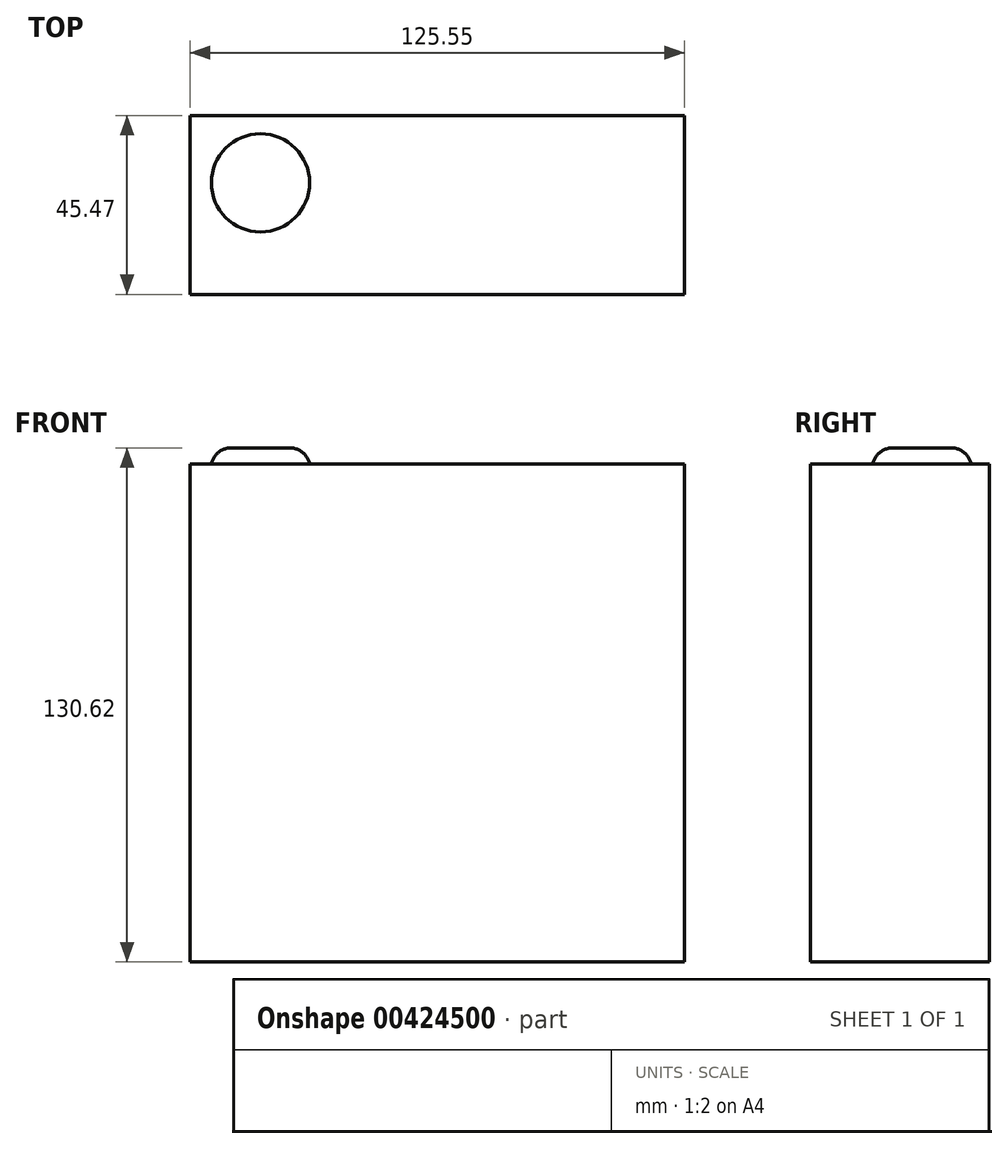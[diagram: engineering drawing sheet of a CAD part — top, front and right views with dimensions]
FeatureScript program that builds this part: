
annotation { "Feature Type Name" : "Feature", "Feature Type Description" : "" }
export const myFeature = defineFeature(function(context is Context, id is Id, definition is map)
    precondition{}
    {
        {
            var Q0;
            Q0=qCreatedBy(makeId("Front.planeOp"),FACE);
            var sketch = newSketch(context, id + "F0", { "sketchPlane" : qUnion([Q0])});
            skLineSegment(sketch, "E0.bottom", {"start": v(-59.76, 61.14) * mm, "end": v(65.8, 61.14) * mm});
            skLineSegment(sketch, "E0.top", {"start": v(-59.76, -65.42) * mm, "end": v(65.8, -65.42) * mm});
            skLineSegment(sketch, "E0.left", {"start": v(-59.76, 61.14) * mm, "end": v(-59.76, -65.42) * mm});
            skLineSegment(sketch, "E0.right", {"start": v(65.8, 61.14) * mm, "end": v(65.8, -65.42) * mm});
            skSolve(sketch);
        }
        {
            var Q0;
            Q0 = qSketchRegion(id + "F0", true);
            extrude(context, id + "F1", {"entities" : qUnion([Q0]), "depth" : 45.47 * mm});
        }
        {
            var Q0;
            Q0=makeQuery(id+"F1.opExtrude","SWEPT_FACE",FACE,{"disambiguationData":[OSD([sQuery(id+"F0.wireOp",EDGE,"E0.bottom")])]});
            var sketch = newSketch(context, id + "F2", { "sketchPlane" : qUnion([Q0])});
            skCircle(sketch, "E1", {"center": v(-41.9, -17.1) * mm, "radius": 12.47 * mm});
            skSolve(sketch);
        }
        {
            var Q0;
            Q0 = qSketchRegion(id + "F2", true);
            extrude(context, id + "F3", {"entities" : qUnion([Q0]), "operationType" : NewBodyOperationType.ADD, "depth" : 4.06 * mm});
        }
        {
            var Q0;
            Q0=makeQuery(id+"F3.opExtrude","CAP_FACE",FACE,{"disambiguationData":[OSD([sQuery(id+"F2.wireOp",EDGE,"E1")])],"isStart":false});
            fillet(context, id + "F4", {"entities" : qUnion([Q0]), "radius" : 5.08 * mm, "tangentPropagation" : true, "allowEdgeOverflow" : false});
        }
    });
